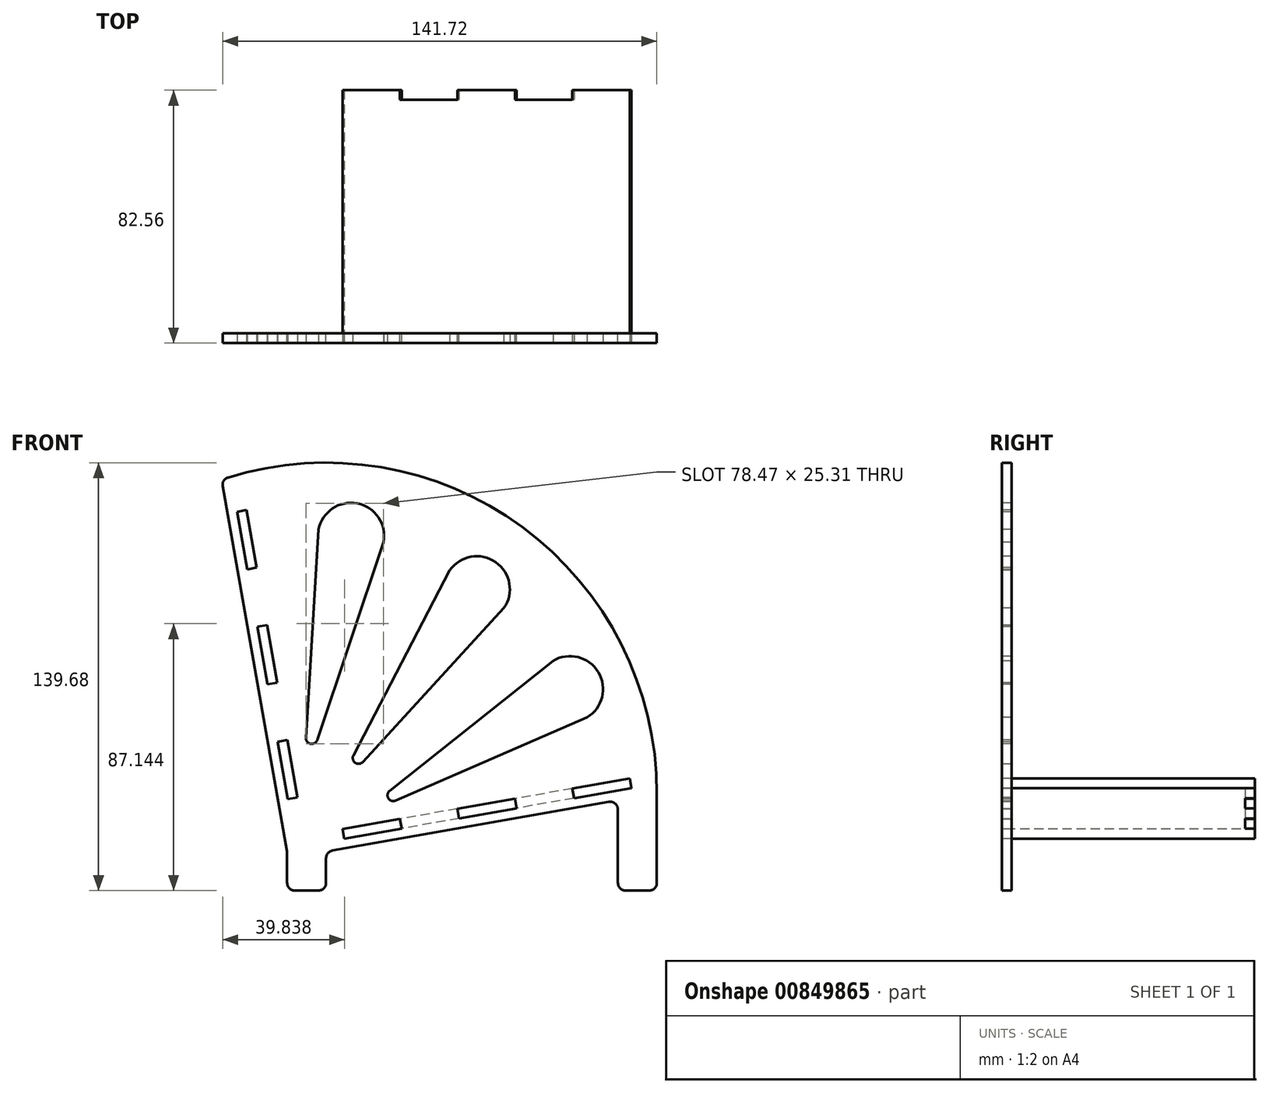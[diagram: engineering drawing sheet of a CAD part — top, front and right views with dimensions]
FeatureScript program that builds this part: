
annotation { "Feature Type Name" : "Feature", "Feature Type Description" : "" }
export const myFeature = defineFeature(function(context is Context, id is Id, definition is map)
    precondition{}
    {
        {
            var Q0;
            Q0=qCreatedBy(makeId("Front.planeOp"),FACE);
            var sketch = newSketch(context, id + "F0", { "sketchPlane" : qUnion([Q0])});
            skLineSegment(sketch, "E0", {"start": v(0, 0) * mm, "end": v(12.7, 0) * mm});
            skLineSegment(sketch, "E1", {"start": v(12.7, 0) * mm, "end": v(12.7, 12.7) * mm});
            skLineSegment(sketch, "E2", {"start": v(12.7, 12.7) * mm, "end": v(107.95, 29.5) * mm});
            skLineSegment(sketch, "E3", {"start": v(107.95, 29.5) * mm, "end": v(107.95, 0) * mm});
            skLineSegment(sketch, "E4", {"start": v(107.95, 0) * mm, "end": v(120.65, 0) * mm});
            skLineSegment(sketch, "E5", {"start": v(120.65, 0) * mm, "end": v(120.65, 31.73) * mm});
            skLineSegment(sketch, "E6", {"start": v(0, 0) * mm, "end": v(0, 12.7) * mm});
            skLineSegment(sketch, "E7", {"start": v(0, 12.7) * mm, "end": v(-21.42, 134.15) * mm});
            skPoint(sketch, "E8", {"position": v(12.7, 31.73) * mm});
            skArc(sketch, "E9", {"start": v(-21.42, 134.15) * mm, "mid": v(75.83, 119.3) * mm, "end": v(120.65, 31.73) * mm});
            skLineSegment(sketch, "E10", {"start": v(107.95, 29.5) * mm, "end": v(120.65, 31.73) * mm, "construction": true});
            skSolve(sketch);
        }
        {
            var Q0;
            Q0 = qSketchRegion(id + "F0", true);
            extrude(context, id + "F1", {"entities" : qUnion([Q0]), "depth" : 3.17 * mm, "offsetDistance" : 25.4 * mm});
        }
        {
            var Q0;
            Q0=makeQuery(id+"F1.opExtrude","CAP_FACE",FACE,{"disambiguationData":[OSD([sQuery(id+"F0.wireOp",EDGE,"E0"),sQuery(id+"F0.wireOp",EDGE,"E1"),sQuery(id+"F0.wireOp",EDGE,"E2"),sQuery(id+"F0.wireOp",EDGE,"E3"),sQuery(id+"F0.wireOp",EDGE,"E4"),sQuery(id+"F0.wireOp",EDGE,"E5"),sQuery(id+"F0.wireOp",EDGE,"E6"),sQuery(id+"F0.wireOp",EDGE,"E7"),sQuery(id+"F0.wireOp",EDGE,"E9")])],"isStart":false});
            var sketch = newSketch(context, id + "F2", { "sketchPlane" : qUnion([Q0])});
            skLineSegment(sketch, "E11.bottom", {"start": v(18.04, 20.09) * mm, "end": v(36.8, 23.4) * mm});
            skLineSegment(sketch, "E11.top", {"start": v(18.6, 16.96) * mm, "end": v(37.35, 20.27) * mm});
            skLineSegment(sketch, "E11.left", {"start": v(18.04, 20.09) * mm, "end": v(18.6, 16.96) * mm});
            skLineSegment(sketch, "E11.right", {"start": v(36.8, 23.4) * mm, "end": v(37.35, 20.27) * mm});
            skLineSegment(sketch, "E12.1.0.0", {"start": v(55.56, 26.7) * mm, "end": v(74.32, 30.01) * mm});
            skLineSegment(sketch, "E12.1.0.1", {"start": v(56.11, 23.58) * mm, "end": v(74.87, 26.89) * mm});
            skLineSegment(sketch, "E12.1.0.2", {"start": v(55.56, 26.7) * mm, "end": v(56.11, 23.58) * mm});
            skLineSegment(sketch, "E12.1.0.3", {"start": v(74.32, 30.01) * mm, "end": v(74.87, 26.89) * mm});
            skLineSegment(sketch, "E12.2.0.0", {"start": v(93.08, 33.32) * mm, "end": v(111.84, 36.63) * mm});
            skLineSegment(sketch, "E12.2.0.1", {"start": v(93.63, 30.2) * mm, "end": v(112.4, 33.5) * mm});
            skLineSegment(sketch, "E12.2.0.2", {"start": v(93.08, 33.32) * mm, "end": v(93.63, 30.2) * mm});
            skLineSegment(sketch, "E12.2.0.3", {"start": v(111.84, 36.63) * mm, "end": v(112.4, 33.5) * mm});
            skLineSegment(sketch, "E12.direction1", {"start": v(18.6, 16.96) * mm, "end": v(56.11, 23.58) * mm, "construction": true});
            skLineSegment(sketch, "E13", {"start": v(107.95, 29.5) * mm, "end": v(0.38, 10.53) * mm, "construction": true});
            skLineSegment(sketch, "E14", {"start": v(-21.42, 134.15) * mm, "end": v(0.38, 10.53) * mm, "construction": true});
            skPoint(sketch, "E15", {"position": v(0.38, 10.53) * mm});
            skLineSegment(sketch, "E16", {"start": v(0.38, 10.53) * mm, "end": v(76.3, 118.96) * mm, "construction": true});
            skLineSegment(sketch, "E17.MirrorCS", {"start": v(-3.29, 67.91) * mm, "end": v(-6.41, 67.36) * mm});
            skLineSegment(sketch, "E18.MirrorCS", {"start": v(3.33, 30.4) * mm, "end": v(0.2, 29.84) * mm});
            skLineSegment(sketch, "E19.MirrorCS", {"start": v(-6.6, 86.67) * mm, "end": v(-9.72, 86.12) * mm});
            skLineSegment(sketch, "E20.MirrorCS", {"start": v(-9.9, 105.43) * mm, "end": v(-13.03, 104.88) * mm});
            skLineSegment(sketch, "E21.MirrorCS", {"start": v(-13.21, 124.2) * mm, "end": v(-16.34, 123.64) * mm});
            skLineSegment(sketch, "E22.MirrorCS", {"start": v(0.02, 49.15) * mm, "end": v(-3.1, 48.6) * mm});
            skLineSegment(sketch, "E23.MirrorCS", {"start": v(0.2, 29.84) * mm, "end": v(-3.1, 48.6) * mm});
            skLineSegment(sketch, "E24.MirrorCS", {"start": v(-3.29, 67.91) * mm, "end": v(-6.6, 86.67) * mm});
            skLineSegment(sketch, "E25.MirrorCS", {"start": v(-9.9, 105.43) * mm, "end": v(-13.21, 124.2) * mm});
            skLineSegment(sketch, "E26.MirrorCS", {"start": v(-6.41, 67.36) * mm, "end": v(-9.72, 86.12) * mm});
            skLineSegment(sketch, "E27.MirrorCS", {"start": v(3.33, 30.4) * mm, "end": v(0.02, 49.15) * mm});
            skLineSegment(sketch, "E28.MirrorCS", {"start": v(-13.03, 104.88) * mm, "end": v(-16.34, 123.64) * mm});
            skLineSegment(sketch, "E29", {"start": v(21.63, 44.17) * mm, "end": v(53.07, 104.56) * mm});
            skLineSegment(sketch, "E30", {"start": v(24.73, 42) * mm, "end": v(70.72, 92.2) * mm});
            skArc(sketch, "E31", {"start": v(70.72, 92.2) * mm, "mid": v(68.08, 107.2) * mm, "end": v(53.07, 104.56) * mm});
            skLineSegment(sketch, "E32", {"start": v(53.07, 104.56) * mm, "end": v(70.72, 92.2) * mm, "construction": true});
            skPoint(sketch, "E33.visualSharp", {"position": v(14.95, 31.33) * mm});
            skArc(sketch, "E33.filletArc", {"start": v(21.63, 44.17) * mm, "mid": v(22.23, 41.73) * mm, "end": v(24.73, 42) * mm});
            skLineSegment(sketch, "E34.1.0", {"start": v(33.48, 32.62) * mm, "end": v(86.76, 75) * mm});
            skLineSegment(sketch, "E34.1.1", {"start": v(86.76, 75) * mm, "end": v(97.86, 56.53) * mm, "construction": true});
            skLineSegment(sketch, "E34.1.2", {"start": v(35.42, 29.38) * mm, "end": v(97.86, 56.53) * mm});
            skArc(sketch, "E34.1.3", {"start": v(97.86, 56.53) * mm, "mid": v(101.54, 71.31) * mm, "end": v(86.76, 75) * mm});
            skArc(sketch, "E34.1.4", {"start": v(33.48, 32.62) * mm, "mid": v(33.03, 30.15) * mm, "end": v(35.42, 29.38) * mm});
            skLineSegment(sketch, "E34.anchor1", {"start": v(0.38, 10.53) * mm, "end": v(21.63, 44.17) * mm, "construction": true});
            skLineSegment(sketch, "E34.anchor2", {"start": v(0.38, 10.53) * mm, "end": v(33.48, 32.62) * mm, "construction": true});
            skLineSegment(sketch, "E35.1.0", {"start": v(6.11, 49.9) * mm, "end": v(10.27, 117.86) * mm});
            skLineSegment(sketch, "E35.1.1", {"start": v(10.27, 117.86) * mm, "end": v(31.42, 113.75) * mm, "construction": true});
            skLineSegment(sketch, "E35.1.2", {"start": v(9.82, 49.18) * mm, "end": v(31.42, 113.75) * mm});
            skArc(sketch, "E35.1.3", {"start": v(31.42, 113.75) * mm, "mid": v(22.9, 126.38) * mm, "end": v(10.27, 117.86) * mm});
            skArc(sketch, "E35.1.4", {"start": v(6.11, 49.9) * mm, "mid": v(7.65, 47.92) * mm, "end": v(9.82, 49.18) * mm});
            skSolve(sketch);
        }
        {
            var Q0;
            Q0 = qSketchRegion(id + "F2", true);
            extrude(context, id + "F3", {"entities" : qUnion([Q0]), "operationType" : NewBodyOperationType.REMOVE, "endBound" : BoundingType.THROUGH_ALL, "oppositeDirection" : true, "depth" : 25.4 * mm, "offsetDistance" : 25.4 * mm});
        }
        {
            var Q0;
            Q0=makeQuery(id+"F3.boolean.opBoolean","COPY",FACE,{"derivedFrom":makeQuery(id+"F3.opExtrude","SWEPT_FACE",FACE,{"disambiguationData":[OSD([sQuery(id+"F2.wireOp",EDGE,"E12.2.0.1")])]})});
            var sketch = newSketch(context, id + "F4", { "sketchPlane" : qUnion([Q0])});
            skLineSegment(sketch, "E36.bottom", {"start": v(116.5, -3.18) * mm, "end": v(97.46, -3.18) * mm});
            skLineSegment(sketch, "E36.top", {"start": v(116.5, 0) * mm, "end": v(97.46, 0) * mm, "construction": true});
            skLineSegment(sketch, "E36.left", {"start": v(116.5, -3.18) * mm, "end": v(116.5, 0) * mm});
            skLineSegment(sketch, "E36.right", {"start": v(97.46, -3.18) * mm, "end": v(97.46, 0) * mm});
            skLineSegment(sketch, "E37.bottom", {"start": v(78.4, -3.18) * mm, "end": v(59.36, -3.18) * mm});
            skLineSegment(sketch, "E37.top", {"start": v(78.4, 0) * mm, "end": v(59.36, 0) * mm, "construction": true});
            skLineSegment(sketch, "E37.left", {"start": v(78.4, -3.18) * mm, "end": v(78.4, 0) * mm});
            skLineSegment(sketch, "E37.right", {"start": v(59.36, -3.18) * mm, "end": v(59.36, 0) * mm});
            skLineSegment(sketch, "E38.bottom", {"start": v(40.3, -3.18) * mm, "end": v(21.26, -3.18) * mm});
            skLineSegment(sketch, "E38.top", {"start": v(40.3, 0) * mm, "end": v(21.26, 0) * mm, "construction": true});
            skLineSegment(sketch, "E38.left", {"start": v(40.3, -3.18) * mm, "end": v(40.3, 0) * mm});
            skLineSegment(sketch, "E38.right", {"start": v(21.26, -3.18) * mm, "end": v(21.26, 0) * mm});
            skLineSegment(sketch, "E39", {"start": v(97.46, 0) * mm, "end": v(78.4, 0) * mm});
            skLineSegment(sketch, "E40", {"start": v(59.36, 0) * mm, "end": v(40.3, 0) * mm});
            skLineSegment(sketch, "E41", {"start": v(21.26, 0) * mm, "end": v(21.26, 38.1) * mm});
            skLineSegment(sketch, "E42", {"start": v(21.26, 38.1) * mm, "end": v(116.5, 38.1) * mm, "construction": true});
            skLineSegment(sketch, "E43", {"start": v(116.5, 38.1) * mm, "end": v(116.5, 0) * mm});
            skLineSegment(sketch, "E44.MirrorCS", {"start": v(116.5, 79.38) * mm, "end": v(116.5, 76.2) * mm});
            skLineSegment(sketch, "E45.MirrorCS", {"start": v(40.3, 79.37) * mm, "end": v(40.3, 76.2) * mm});
            skLineSegment(sketch, "E46.MirrorCS", {"start": v(59.36, 79.38) * mm, "end": v(59.36, 76.2) * mm});
            skLineSegment(sketch, "E47.MirrorCS", {"start": v(97.46, 79.38) * mm, "end": v(97.46, 76.2) * mm});
            skLineSegment(sketch, "E48.MirrorCS", {"start": v(21.26, 79.37) * mm, "end": v(21.26, 76.2) * mm});
            skLineSegment(sketch, "E49.MirrorCS", {"start": v(78.4, 79.37) * mm, "end": v(78.4, 76.2) * mm});
            skLineSegment(sketch, "E50.MirrorCS", {"start": v(21.26, 76.2) * mm, "end": v(21.26, 38.1) * mm});
            skLineSegment(sketch, "E51.MirrorCS", {"start": v(40.3, 76.2) * mm, "end": v(21.26, 76.2) * mm, "construction": true});
            skLineSegment(sketch, "E52.MirrorCS", {"start": v(78.4, 76.2) * mm, "end": v(59.36, 76.2) * mm, "construction": true});
            skLineSegment(sketch, "E53.MirrorCS", {"start": v(116.5, 76.2) * mm, "end": v(97.46, 76.2) * mm, "construction": true});
            skLineSegment(sketch, "E54.MirrorCS", {"start": v(97.46, 76.2) * mm, "end": v(78.4, 76.2) * mm});
            skLineSegment(sketch, "E55.MirrorCS", {"start": v(116.5, 79.38) * mm, "end": v(97.46, 79.38) * mm});
            skLineSegment(sketch, "E56.MirrorCS", {"start": v(40.3, 79.37) * mm, "end": v(21.26, 79.37) * mm});
            skLineSegment(sketch, "E57.MirrorCS", {"start": v(116.5, 38.1) * mm, "end": v(116.5, 76.2) * mm});
            skLineSegment(sketch, "E58.MirrorCS", {"start": v(78.4, 79.37) * mm, "end": v(59.36, 79.37) * mm});
            skLineSegment(sketch, "E59.MirrorCS", {"start": v(59.36, 76.2) * mm, "end": v(40.3, 76.2) * mm});
            skSolve(sketch);
        }
        {
            var Q0;
            Q0 = qSketchRegion(id + "F4", true);
            extrude(context, id + "F5", {"entities" : qUnion([Q0]), "depth" : 3.17 * mm, "offsetDistance" : 25.4 * mm});
        }
        {
            var Q0;
            Q0=makeQuery(id+"F1.opExtrude","SWEPT_EDGE",EDGE,{"disambiguationData":[OSD([sQuery(id+"F0.wireOp",EDGE,"E0"),sQuery(id+"F0.wireOp",EDGE,"E6")])]});
            var Q1;
            Q1=makeQuery(id+"F1.opExtrude","SWEPT_EDGE",EDGE,{"disambiguationData":[OSD([sQuery(id+"F0.wireOp",EDGE,"E4"),sQuery(id+"F0.wireOp",EDGE,"E5")])]});
            var Q2;
            Q2=makeQuery(id+"F1.opExtrude","SWEPT_EDGE",EDGE,{"disambiguationData":[OSD([sQuery(id+"F0.wireOp",EDGE,"E3"),sQuery(id+"F0.wireOp",EDGE,"E4")])]});
            var Q3;
            Q3=makeQuery(id+"F1.opExtrude","SWEPT_EDGE",EDGE,{"disambiguationData":[OSD([sQuery(id+"F0.wireOp",EDGE,"E0"),sQuery(id+"F0.wireOp",EDGE,"E1")])]});
            var Q4;
            Q4=makeQuery(id+"F1.opExtrude","SWEPT_EDGE",EDGE,{"disambiguationData":[OSD([sQuery(id+"F0.wireOp",EDGE,"E1"),sQuery(id+"F0.wireOp",EDGE,"E2")])]});
            var Q5;
            Q5=makeQuery(id+"F1.opExtrude","SWEPT_EDGE",EDGE,{"disambiguationData":[OSD([sQuery(id+"F0.wireOp",EDGE,"E2"),sQuery(id+"F0.wireOp",EDGE,"E3")])]});
            var Q6;
            Q6=makeQuery(id+"F1.opExtrude","SWEPT_EDGE",EDGE,{"disambiguationData":[OSD([sQuery(id+"F0.wireOp",EDGE,"E6"),sQuery(id+"F0.wireOp",EDGE,"E7")])]});
            var Q7;
            Q7=makeQuery(id+"F1.opExtrude","SWEPT_EDGE",EDGE,{"disambiguationData":[OSD([sQuery(id+"F0.wireOp",EDGE,"E7"),sQuery(id+"F0.wireOp",EDGE,"E9")])]});
            fillet(context, id + "F6", {"entities" : qUnion([Q0, Q1, Q2, Q3, Q4, Q5, Q6, Q7]), "radius" : 2.54 * mm, "tangentPropagation" : true, "allowEdgeOverflow" : false});
        }
    });
